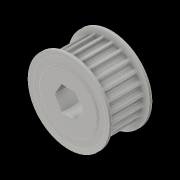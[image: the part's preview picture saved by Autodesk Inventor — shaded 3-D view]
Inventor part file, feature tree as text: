
AUTODESK INVENTOR PART (.ipt)
format: ipt  version: 2016 (Build 200138000, 138)  size: 876,032 bytes
history: native  units: in
note: dims shown in document units (in); Inventor stores cm internally (conversion verified against a paired STEP export)
features: mirror x1
ambient origin geometry x8: Origin, YZ Plane, XZ Plane, XY Plane, X Axis, Y Axis, Z Axis, Center Point
bodies: Solid1 (feature_tree)
feature tree (1):
  mirror  "Mirror1"
